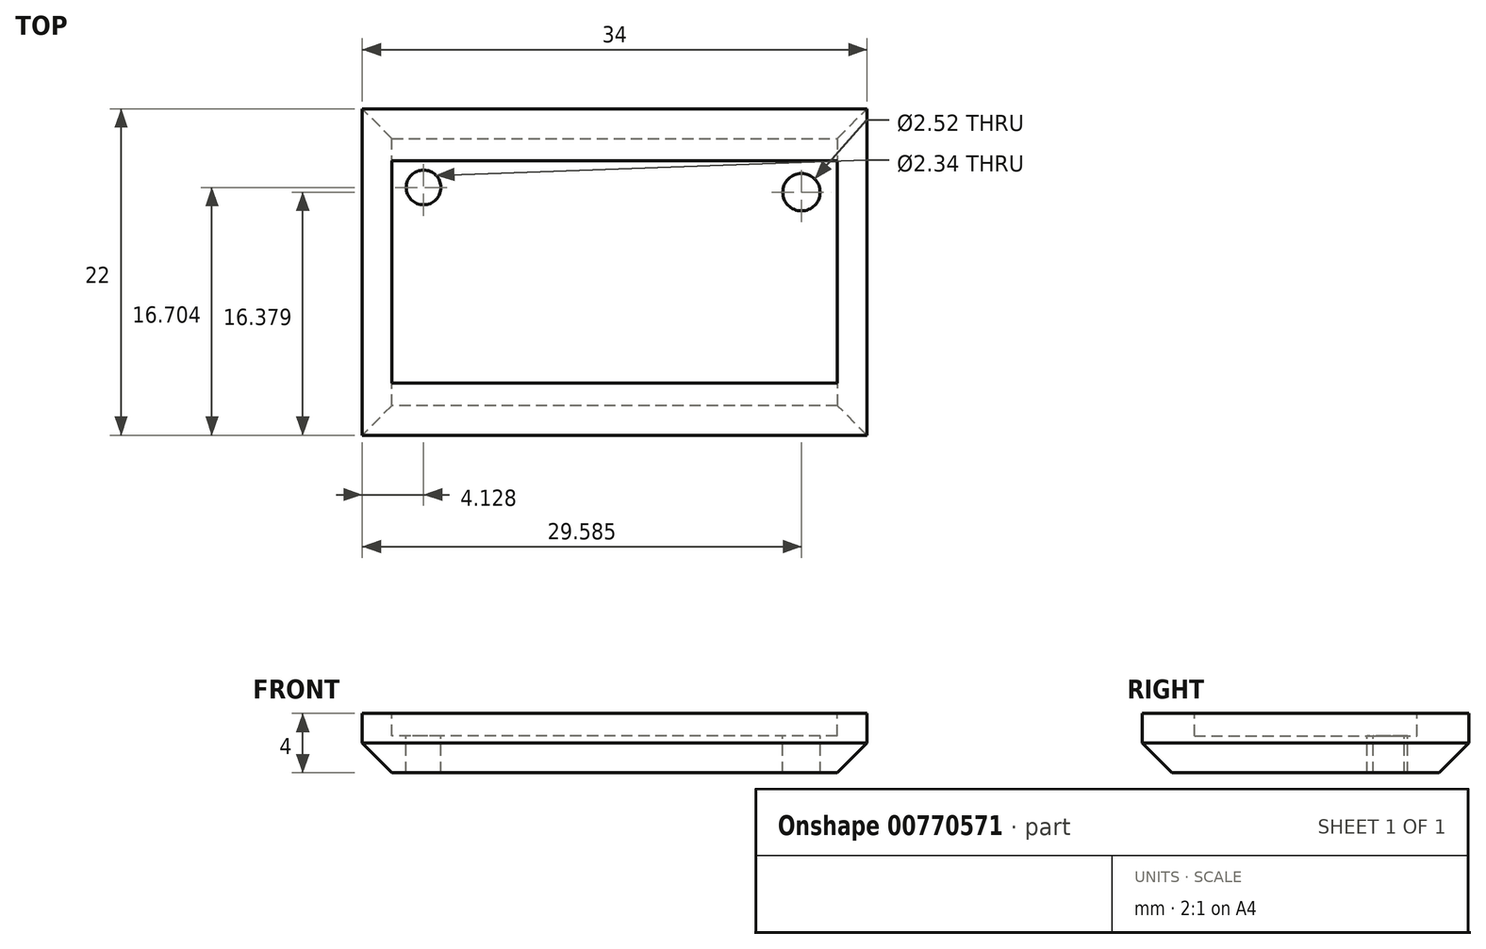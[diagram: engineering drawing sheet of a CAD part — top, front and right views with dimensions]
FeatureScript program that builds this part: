
annotation { "Feature Type Name" : "Feature", "Feature Type Description" : "" }
export const myFeature = defineFeature(function(context is Context, id is Id, definition is map)
    precondition{}
    {
        {
            var Q0;
            Q0=qCreatedBy(makeId("Top.planeOp"),FACE);
            var sketch = newSketch(context, id + "F0", { "sketchPlane" : qUnion([Q0])});
            skLineSegment(sketch, "E0.bottom", {"start": v(17, -11) * mm, "end": v(-17, -11) * mm});
            skLineSegment(sketch, "E0.top", {"start": v(17, 11) * mm, "end": v(-17, 11) * mm});
            skLineSegment(sketch, "E0.left", {"start": v(17, -11) * mm, "end": v(17, 11) * mm});
            skLineSegment(sketch, "E0.right", {"start": v(-17, -11) * mm, "end": v(-17, 11) * mm});
            skPoint(sketch, "E0.middle", {"position": v(0, 0) * mm});
            skSolve(sketch);
        }
        {
            var Q0;
            Q0=makeQuery(id+"F0.imprint","IMPRINT",FACE,{"disambiguationData":[TD([[makeQuery(id+"F0.imprint","IMPRINT",EDGE,{"derivedFrom":sQuery(id+"F0.wireOp",EDGE,"E0.bottom")}),-1.0]])]});
            extrude(context, id + "F1", {"entities" : qUnion([Q0]), "depth" : 4 * mm, "offsetDistance" : 25 * mm});
        }
        {
            var Q0;
            Q0=makeQuery(id+"F1.opExtrude","CAP_EDGE",EDGE,{"disambiguationData":[OSD([sQuery(id+"F0.wireOp",EDGE,"E0.right")])],"isStart":true});
            var Q1;
            Q1=makeQuery(id+"F1.opExtrude","CAP_EDGE",EDGE,{"disambiguationData":[OSD([sQuery(id+"F0.wireOp",EDGE,"E0.left")])],"isStart":true});
            var Q2;
            Q2=makeQuery(id+"F1.opExtrude","CAP_EDGE",EDGE,{"disambiguationData":[OSD([sQuery(id+"F0.wireOp",EDGE,"E0.top")])],"isStart":true});
            var Q3;
            Q3=makeQuery(id+"F1.opExtrude","CAP_EDGE",EDGE,{"disambiguationData":[OSD([sQuery(id+"F0.wireOp",EDGE,"E0.bottom")])],"isStart":true});
            chamfer(context, id + "F2", {"entities" : qUnion([Q0, Q1, Q2, Q3]), "width" : 2 * mm, "tangentPropagation" : true});
        }
        {
            var Q0;
            Q0=makeQuery(id+"F1.opExtrude","CAP_FACE",FACE,{"disambiguationData":[OSD([sQuery(id+"F0.wireOp",EDGE,"E0.bottom"),sQuery(id+"F0.wireOp",EDGE,"E0.top"),sQuery(id+"F0.wireOp",EDGE,"E0.left"),sQuery(id+"F0.wireOp",EDGE,"E0.right")])],"isStart":false});
            var sketch = newSketch(context, id + "F3", { "sketchPlane" : qUnion([Q0])});
            skLineSegment(sketch, "E1.bottom", {"start": v(15, -7.5) * mm, "end": v(-15, -7.5) * mm});
            skLineSegment(sketch, "E1.top", {"start": v(15, 7.5) * mm, "end": v(-15, 7.5) * mm});
            skLineSegment(sketch, "E1.left", {"start": v(15, -7.5) * mm, "end": v(15, 7.5) * mm});
            skLineSegment(sketch, "E1.right", {"start": v(-15, -7.5) * mm, "end": v(-15, 7.5) * mm});
            skPoint(sketch, "E1.middle", {"position": v(0, 0) * mm});
            skSolve(sketch);
        }
        {
            var Q0;
            Q0=makeQuery(id+"F3.imprint","IMPRINT",FACE,{"disambiguationData":[TD([[makeQuery(id+"F3.imprint","IMPRINT",EDGE,{"derivedFrom":sQuery(id+"F3.wireOp",EDGE,"E1.bottom")}),-1.0]])]});
            extrude(context, id + "F4", {"entities" : qUnion([Q0]), "operationType" : NewBodyOperationType.REMOVE, "oppositeDirection" : true, "depth" : 1.5 * mm, "offsetDistance" : 25 * mm});
        }
        {
            var Q0;
            Q0=makeQuery(id+"F4.boolean.opBoolean","COPY",FACE,{"derivedFrom":makeQuery(id+"F4.opExtrude","CAP_FACE",FACE,{"disambiguationData":[OSD([sQuery(id+"F3.wireOp",EDGE,"E1.bottom"),sQuery(id+"F3.wireOp",EDGE,"E1.top"),sQuery(id+"F3.wireOp",EDGE,"E1.left"),sQuery(id+"F3.wireOp",EDGE,"E1.right")])],"isStart":false})});
            var sketch = newSketch(context, id + "F5", { "sketchPlane" : qUnion([Q0])});
            skCircle(sketch, "E2", {"center": v(-12.87, 5.7) * mm, "radius": 1.17 * mm});
            skCircle(sketch, "E3", {"center": v(12.58, 5.38) * mm, "radius": 1.26 * mm});
            skSolve(sketch);
        }
        {
            var Q0;
            Q0=makeQuery(id+"F5.imprint","IMPRINT",FACE,{"disambiguationData":[TD([[makeQuery(id+"F5.imprint","IMPRINT",EDGE,{"derivedFrom":sQuery(id+"F5.wireOp",EDGE,"E2")}),1.0]])]});
            var Q1;
            Q1=makeQuery(id+"F5.imprint","IMPRINT",FACE,{"disambiguationData":[TD([[makeQuery(id+"F5.imprint","IMPRINT",EDGE,{"derivedFrom":sQuery(id+"F5.wireOp",EDGE,"E3")}),1.0]])]});
            extrude(context, id + "F6", {"entities" : qUnion([Q0, Q1]), "operationType" : NewBodyOperationType.REMOVE, "oppositeDirection" : true, "depth" : 25 * mm, "offsetDistance" : 25 * mm});
        }
    });
